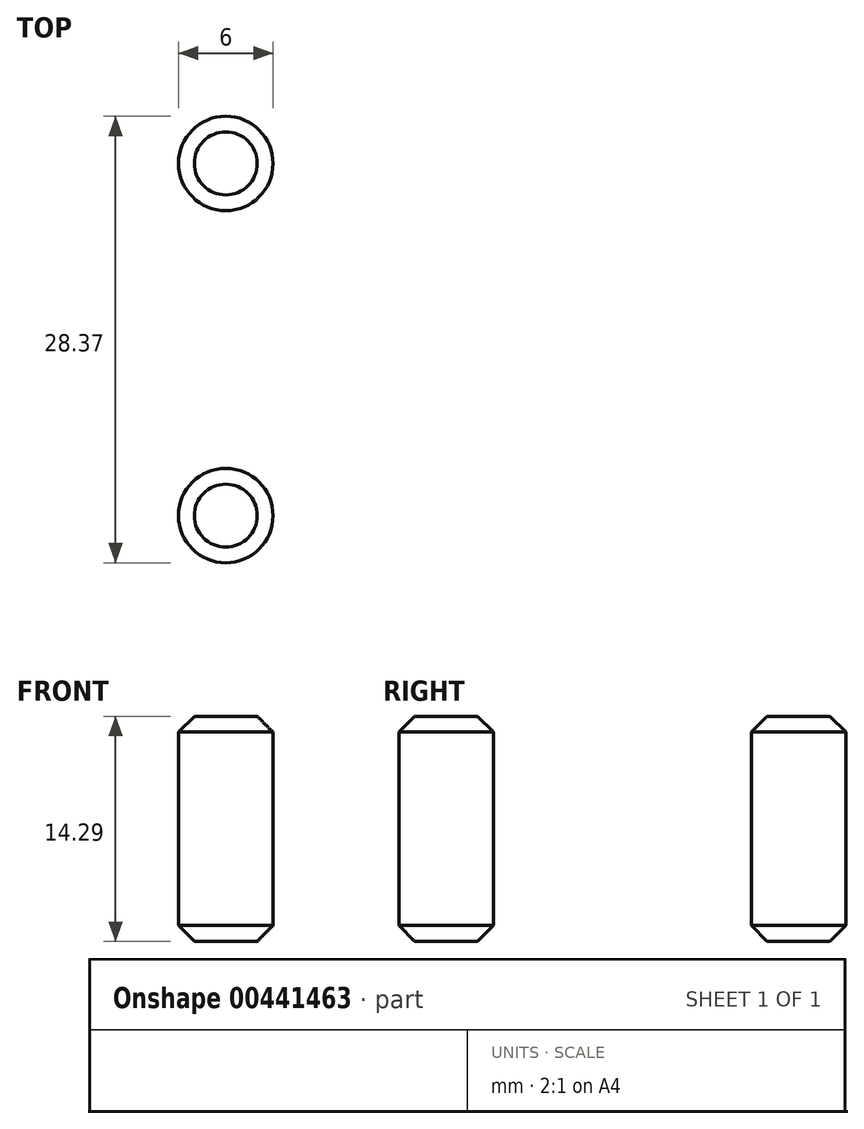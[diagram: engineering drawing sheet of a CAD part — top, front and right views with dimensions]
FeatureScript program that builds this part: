
annotation { "Feature Type Name" : "Feature", "Feature Type Description" : "" }
export const myFeature = defineFeature(function(context is Context, id is Id, definition is map)
    precondition{}
    {
        {
            var Q0;
            Q0=qCreatedBy(makeId("Top.planeOp"),FACE);
            var sketch = newSketch(context, id + "F0", { "sketchPlane" : qUnion([Q0])});
            skCircle(sketch, "E0", {"center": v(0, 0) * mm, "radius": 3 * mm});
            skCircle(sketch, "E1", {"center": v(0, 22.37) * mm, "radius": 3 * mm});
            skSolve(sketch);
        }
        {
            var Q0;
            Q0 = qSketchRegion(id + "F0", true);
            extrude(context, id + "F1", {"entities" : qUnion([Q0]), "depth" : 14.29 * mm});
        }
        {
            var Q0;
            Q0=makeQuery(id+"F1.opExtrude","CAP_EDGE",EDGE,{"disambiguationData":[OSD([sQuery(id+"F0.wireOp",EDGE,"E1")])],"isStart":true});
            var Q1;
            Q1=makeQuery(id+"F1.opExtrude","CAP_EDGE",EDGE,{"disambiguationData":[OSD([sQuery(id+"F0.wireOp",EDGE,"E1")])],"isStart":false});
            var Q2;
            Q2=makeQuery(id+"F1.opExtrude","CAP_EDGE",EDGE,{"disambiguationData":[OSD([sQuery(id+"F0.wireOp",EDGE,"E0")])],"isStart":true});
            var Q3;
            Q3=makeQuery(id+"F1.opExtrude","CAP_EDGE",EDGE,{"disambiguationData":[OSD([sQuery(id+"F0.wireOp",EDGE,"E0")])],"isStart":false});
            chamfer(context, id + "F2", {"entities" : qUnion([Q0, Q1, Q2, Q3]), "width" : 1 * mm, "tangentPropagation" : true});
        }
    });
